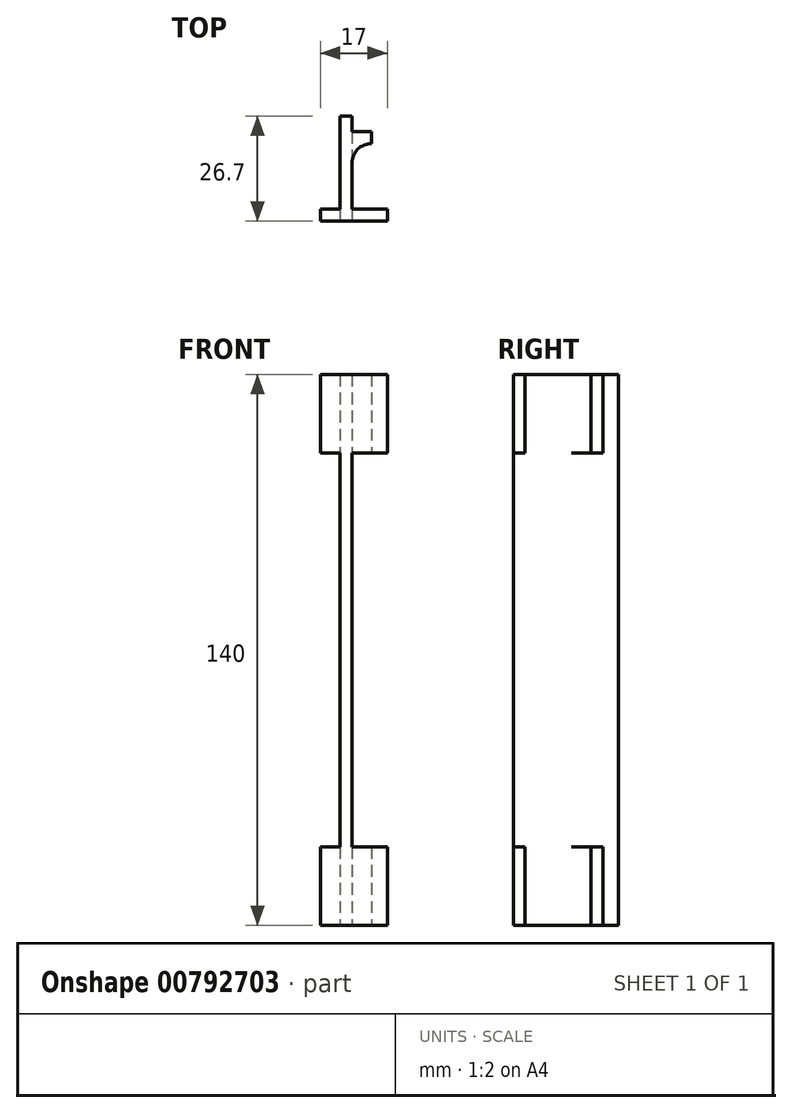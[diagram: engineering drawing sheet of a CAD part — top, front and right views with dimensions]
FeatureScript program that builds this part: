
annotation { "Feature Type Name" : "Feature", "Feature Type Description" : "" }
export const myFeature = defineFeature(function(context is Context, id is Id, definition is map)
    precondition{}
    {
        {
            var Q0;
            Q0=qCreatedBy(makeId("Top.planeOp"),FACE);
            var sketch = newSketch(context, id + "F0", { "sketchPlane" : qUnion([Q0])});
            skLineSegment(sketch, "E0", {"start": v(0, 0) * mm, "end": v(12, 0) * mm});
            skLineSegment(sketch, "E1", {"start": v(12, 0) * mm, "end": v(12, 3) * mm});
            skLineSegment(sketch, "E2", {"start": v(12, 3) * mm, "end": v(3, 3) * mm});
            skLineSegment(sketch, "E3", {"start": v(3, 3) * mm, "end": v(3, 14.7) * mm});
            skLineSegment(sketch, "E4", {"start": v(8, 19.7) * mm, "end": v(8, 19.7) * mm});
            skLineSegment(sketch, "E5", {"start": v(8, 19.7) * mm, "end": v(8, 22.7) * mm});
            skLineSegment(sketch, "E6", {"start": v(8, 22.7) * mm, "end": v(3, 22.7) * mm});
            skLineSegment(sketch, "E7", {"start": v(3, 22.7) * mm, "end": v(3, 26.7) * mm});
            skLineSegment(sketch, "E8", {"start": v(3, 26.7) * mm, "end": v(0, 26.7) * mm});
            skLineSegment(sketch, "E9", {"start": v(0, 26.7) * mm, "end": v(0, 3) * mm});
            skLineSegment(sketch, "E10", {"start": v(0, 3) * mm, "end": v(-5, 3) * mm});
            skLineSegment(sketch, "E11", {"start": v(-5, 3) * mm, "end": v(-5, 0) * mm});
            skLineSegment(sketch, "E12", {"start": v(-5, 0) * mm, "end": v(0, 0) * mm});
            skPoint(sketch, "E13.visualSharp", {"position": v(3, 19.7) * mm});
            skArc(sketch, "E13.filletArc", {"start": v(8, 19.7) * mm, "mid": v(4.46, 18.24) * mm, "end": v(3, 14.7) * mm});
            skSolve(sketch);
        }
        {
            var Q0;
            Q0=makeQuery(id+"F0.imprint","IMPRINT",FACE,{"disambiguationData":[TD([[makeQuery(id+"F0.imprint","IMPRINT",EDGE,{"derivedFrom":sQuery(id+"F0.wireOp",EDGE,"E0")}),1.0]])]});
            extrude(context, id + "F1", {"entities" : qUnion([Q0]), "depth" : 140 * mm, "offsetDistance" : 25 * mm});
        }
        {
            var Q0;
            Q0=qCreatedBy(makeId("Front.planeOp"),FACE);
            var sketch = newSketch(context, id + "F2", { "sketchPlane" : qUnion([Q0])});
            skLineSegment(sketch, "E14.0", {"start": v(-5, 120) * mm, "end": v(-5, 20) * mm});
            skLineSegment(sketch, "E15.0", {"start": v(3, 140) * mm, "end": v(3, 0) * mm});
            skLineSegment(sketch, "E16.0", {"start": v(12, 120) * mm, "end": v(12, 20) * mm});
            skLineSegment(sketch, "E17", {"start": v(-5, 20) * mm, "end": v(0, 20) * mm});
            skLineSegment(sketch, "E18", {"start": v(0, 20) * mm, "end": v(0, 120) * mm});
            skLineSegment(sketch, "E19", {"start": v(0, 120) * mm, "end": v(-5, 120) * mm});
            skLineSegment(sketch, "E20", {"start": v(-5, 70) * mm, "end": v(12, 70) * mm, "construction": true});
            skLineSegment(sketch, "E21", {"start": v(3, 120) * mm, "end": v(12, 120) * mm});
            skLineSegment(sketch, "E22", {"start": v(3, 20) * mm, "end": v(12, 20) * mm});
            skPoint(sketch, "E23.0.end.orphan", {"position": v(3, 140) * mm});
            skPoint(sketch, "E23.0.start.orphan", {"position": v(12, 140) * mm});
            skPoint(sketch, "E24.0.start.orphan", {"position": v(0, 140) * mm});
            skPoint(sketch, "E25.orphan", {"position": v(-5, 140) * mm});
            skPoint(sketch, "E26.0.end.orphan", {"position": v(-5, 0) * mm});
            skPoint(sketch, "E26.0.start.orphan", {"position": v(0, 0) * mm});
            skPoint(sketch, "E27.0.end.orphan", {"position": v(3, 0) * mm});
            skPoint(sketch, "E28.orphan", {"position": v(12, 0) * mm});
            skLineSegment(sketch, "E29", {"start": v(3, 120) * mm, "end": v(3, 20) * mm});
            skSolve(sketch);
        }
        {
            var Q0;
            Q0=makeQuery(id+"F2.imprint","IMPRINT",FACE,{"disambiguationData":[TD([[makeQuery(id+"F2.imprint","IMPRINT",EDGE,{"derivedFrom":sQuery(id+"F2.wireOp",EDGE,"E14.0")}),1.0]])]});
            var Q1;
            Q1=makeQuery(id+"F2.imprint","IMPRINT",FACE,{"disambiguationData":[TD([[makeQuery(id+"F2.imprint","IMPRINT",EDGE,{"derivedFrom":sQuery(id+"F2.wireOp",EDGE,"E16.0")}),-1.0]])]});
            extrude(context, id + "F3", {"entities" : qUnion([Q0, Q1]), "operationType" : NewBodyOperationType.REMOVE, "oppositeDirection" : true, "depth" : 25 * mm, "offsetDistance" : 25 * mm});
        }
    });
